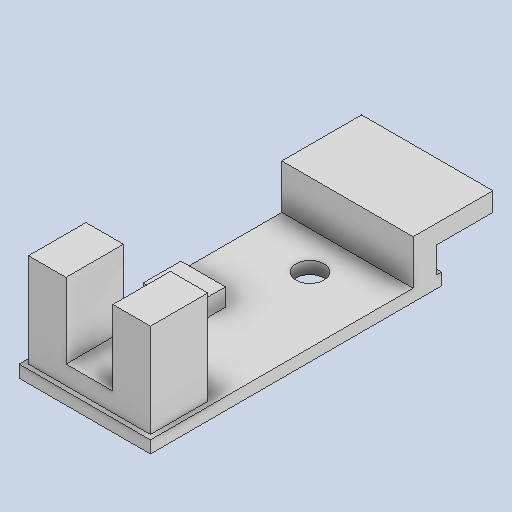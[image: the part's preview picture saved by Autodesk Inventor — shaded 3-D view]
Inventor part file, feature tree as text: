
AUTODESK INVENTOR PART (.ipt)
format: ipt  version: 2022 (Build 260153070, 153G)  size: 138,752 bytes
history: native  units: in
note: dims shown in document units (in); Inventor stores cm internally (conversion verified against a paired STEP export)
features: other x3, sketch x3
ambient origin geometry x8: Origin, YZ Plane, XZ Plane, XY Plane, X Axis, Y Axis, Z Axis, Center Point
bodies: Solid1 (feature_tree)
feature tree (6):
  other  "LM393 encoder.ipt"
  other  "Solid1::LM393 encoder.ipt"
  other  "TaggingFeature1"
  sketch  "Sketch1"  dims[d0=0.3937in]
  sketch  "Sketch2"
  sketch  "Sketch3"
